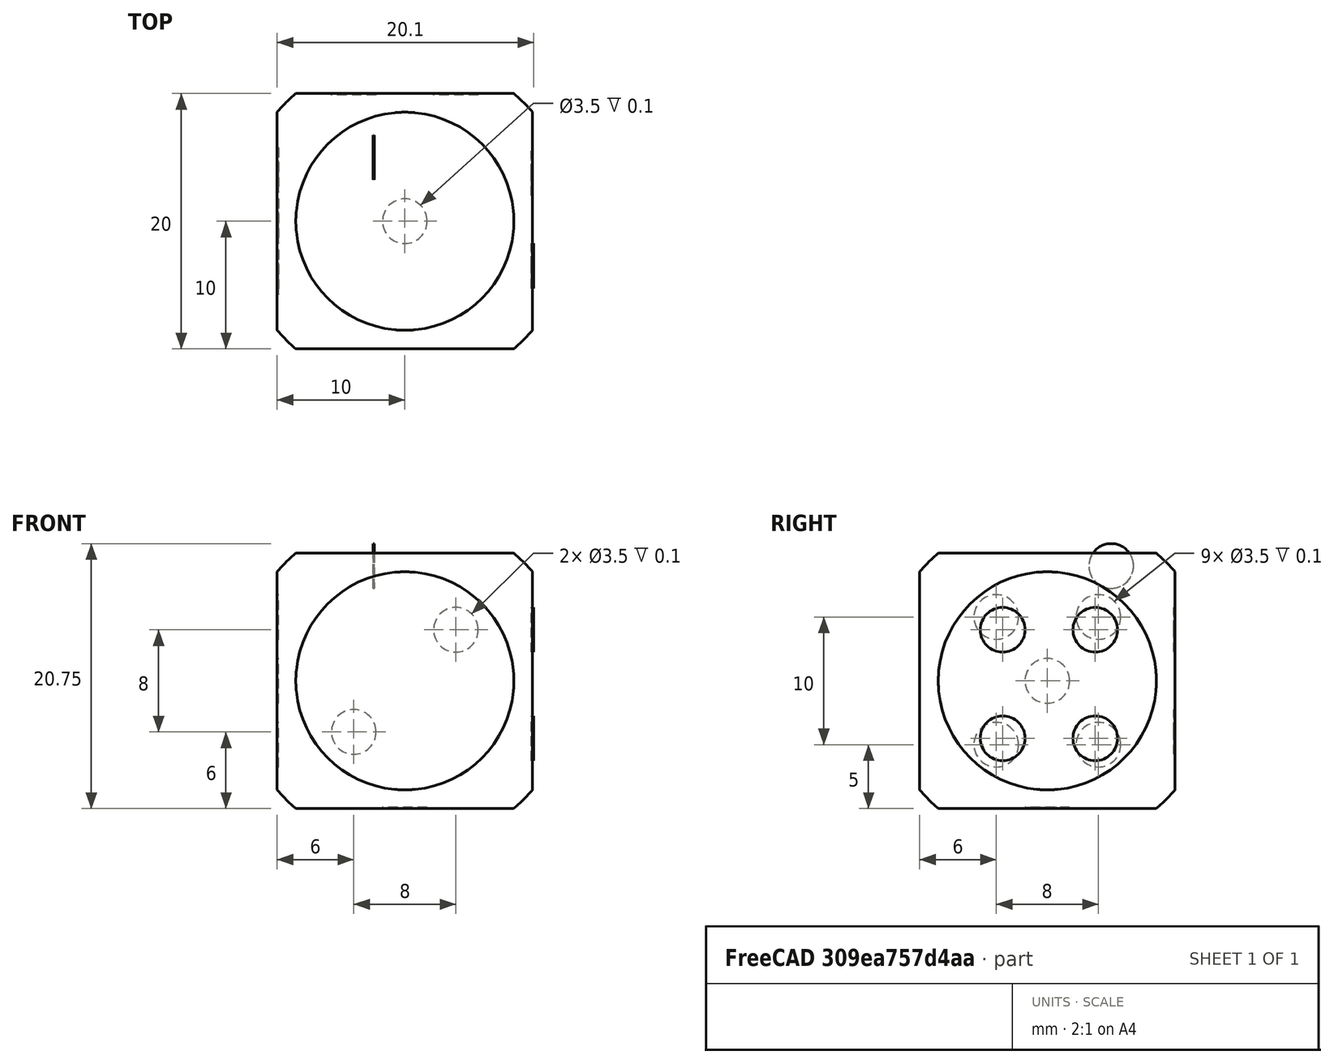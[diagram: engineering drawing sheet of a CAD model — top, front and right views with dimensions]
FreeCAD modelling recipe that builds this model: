
FCSTD DOCUMENT  (FreeCAD 0.21R33694 (Git))
Label: prodriguez_exercici2
License: All rights reserved
LicenseURL: https://en.wikipedia.org/wiki/All_rights_reserved
objects: Part::Cylinder×11, Part::Cut×10, Part::FeaturePython×4, Part::Box×1, Part::Sphere×1, Part::Fillet×1, Part::MultiCommon×1
note: 25 computed .brp shape members not serialized (recipe doc carries the construction recipe); baked Part::Feature solids carry a one-line shape summary decoded from their .brp

FEATURE [Part::Box] Box  label="Cub"
  AttacherType = Attacher::AttachEngine3D
  Height = 20
  Length = 20
  Width = 20
FEATURE [Part::Sphere] Sphere  label="Esfera"
  Angle1 = -90
  Angle2 = 90
  Angle3 = 360
  AttacherType = Attacher::AttachEngine3D
  Placement = pos=(10,10,10) rot=(0,0,1;0rad)
  Radius = 13.15
  expr: .Placement.Base.x = 10
  expr: .Placement.Base.y = 10
  expr: .Placement.Base.z = 10
FEATURE [Part::Fillet] Fillet
  Base = -> Box
  Edges = 12 edges r=1.5: [Edge1,Edge2,Edge3,Edge4,Edge5,Edge6,Edge7,Edge8,Edge9,Edge10,Edge11,Edge12]
FEATURE [Part::Cylinder] Cylinder  label="Cilindre"
  Angle = 360
  AttacherType = Attacher::AttachEngine3D
  FirstAngle = 0
  Height = 0.1
  Placement = pos=(7.5,15,19) rot=(0,1,0;1.5708rad)
  Radius = 1.75
  SecondAngle = 0
  expr: .Placement.Base.x = 7.5
  expr: .Placement.Base.y = 15
  expr: .Placement.Base.z = 19
  expr: .Placement.Rotation.Pitch = 90
  expr: .Placement.Rotation.Roll = 90
  expr: .Placement.Rotation.Yaw = 90
FEATURE [Part::FeaturePython] Array  # Draft array (typed FeaturePython)
  AlwaysSyncPlacement = false
  Angle = 360
  ArrayType = 0
  Axis = (0,0,1)
  Base = -> Cylinder
  Center = (0,0,0)
  Count = 6
  ExpandArray = false
  Fuse = false
  IntervalAxis = (0,0,0)
  IntervalX = (5.5,0,0)
  IntervalY = (0,-5,0)
  IntervalZ = (0,0,100)
  NumberCircles = 3
  NumberPolar = 5
  NumberX = 2
  NumberY = 3
  NumberZ = 1
  Placement = pos=(0,0,1) rot=(0,0,1;0rad)
  PlacementList = 6 placements: [(7.5,15,19),(7.5,10,19),(7.5,5,19),(13,15,19),(13,10,19),(13,5,19)]
  RadialDistance = 50
  ScaleList = (6) [(1,1,1),(1,1,1),(1,1,1),(1,1,1),(1,1,1),(1,1,1)]
  Symmetry = 1
  TangentialDistance = 25
  expr: .Placement.Base.x = 0
  expr: .Placement.Base.z = 1
FEATURE [Part::Cylinder] Cylinder001  label="Cilindre001"
  Angle = 360
  AttacherType = Attacher::AttachEngine3D
  FirstAngle = 0
  Height = 0.1
  Placement = pos=(20,6.5,14) rot=(0,1,0;1.5708rad)
  Radius = 1.75
  SecondAngle = 0
  expr: .Placement.Base.x = 20
  expr: .Placement.Base.y = 6.5
  expr: .Placement.Base.z = 14
  expr: .Placement.Rotation.Pitch = 90
  expr: .Placement.Rotation.Roll = 0
FEATURE [Part::MultiCommon] Common
  Shapes = -> [Sphere,Fillet]
FEATURE [Part::FeaturePython] Array001  # Draft array (typed FeaturePython)
  AlwaysSyncPlacement = false
  Angle = 360
  ArrayType = 0
  Axis = (0,0,1)
  Base = -> Cylinder001
  Center = (0,0,0)
  Count = 8
  ExpandArray = false
  Fuse = false
  IntervalAxis = (0,0,0)
  IntervalX = (0,0,0)
  IntervalY = (0,7.25,0)
  IntervalZ = (0,0,-8.5)
  NumberCircles = 3
  NumberPolar = 5
  NumberX = 2
  NumberY = 2
  NumberZ = 2
  Placement = pos=(-0.1,0,0) rot=(0,0,1;0rad)
  PlacementList = 8 placements: [(20,6.5,14),(20,6.5,5.5),(20,13.75,14),(20,13.75,5.5),(20,6.5,14),(20,6.5,5.5),(20,13.75,14),(20,13.75,5.5)]
  RadialDistance = 50
  ScaleList = (8) [(1,1,1),(1,1,1),(1,1,1),(1,1,1),(1,1,1),(1,1,1),(1,1,1),(1,1,1)]
  Symmetry = 1
  TangentialDistance = 25
  expr: .Placement.Base.x = -0.1
FEATURE [Part::Cut] Cut
  Base = -> Common
  Tool = -> Array
FEATURE [Part::Cut] Cut001
  Base = -> Cut
  Tool = -> Array001
FEATURE [Part::Cylinder] Cylinder002  label="Cilindre002"
  Angle = 360
  AttacherType = Attacher::AttachEngine3D
  FirstAngle = 0
  Height = 0.1
  Placement = pos=(10,0,10) rot=(1,0,0;1.5708rad)
  Radius = 1.75
  SecondAngle = 0
  expr: .Placement.Base.x = 10
  expr: .Placement.Base.y = 0
  expr: .Placement.Base.z = 10
  expr: .Placement.Rotation.Pitch = 0
  expr: .Placement.Rotation.Roll = 90
FEATURE [Part::Cut] Cut002
  Base = -> Cut001
  Tool = -> Cylinder002
FEATURE [Part::Cylinder] Cylinder003  label="Cilindre003"
  Angle = 360
  AttacherType = Attacher::AttachEngine3D
  FirstAngle = 0
  Height = 0.1
  Placement = pos=(6,0,6) rot=(1,0,0;1.5708rad)
  Radius = 1.75
  SecondAngle = 0
  expr: .Placement.Base.x = 6
  expr: .Placement.Base.y = 0
  expr: .Placement.Base.z = 6
  expr: .Placement.Rotation.Roll = 90
FEATURE [Part::Cut] Cut003
  Base = -> Cut002
  Tool = -> Cylinder003
FEATURE [Part::Cylinder] Cylinder004  label="Cilindre004"
  Angle = 360
  AttacherType = Attacher::AttachEngine3D
  FirstAngle = 0
  Height = 0.1
  Placement = pos=(14,0,14) rot=(1,0,0;1.5708rad)
  Radius = 1.75
  SecondAngle = 0
  expr: .Placement.Base.x = 14
  expr: .Placement.Base.z = 14
  expr: .Placement.Rotation.Roll = 90
FEATURE [Part::Cut] Cut004
  Base = -> Cut003
  Tool = -> Cylinder004
FEATURE [Part::Cylinder] Cylinder005  label="Cilindre005"
  Angle = 360
  AttacherType = Attacher::AttachEngine3D
  FirstAngle = 0
  Height = 0.1
  Placement = pos=(10,10,0) rot=(0,0,1;0rad)
  Radius = 1.75
  SecondAngle = 0
  expr: .Placement.Base.x = 10
  expr: .Placement.Base.y = 10
FEATURE [Part::Cut] Cut005
  Base = -> Cut004
  Tool = -> Cylinder005
FEATURE [Part::Cylinder] Cylinder006  label="Cilindre006"
  Angle = 360
  AttacherType = Attacher::AttachEngine3D
  FirstAngle = 0
  Height = 0.1
  Placement = pos=(6,20,6) rot=(1,0,0;1.5708rad)
  Radius = 1.75
  SecondAngle = 0
  expr: .Placement.Base.x = 6
  expr: .Placement.Base.y = 20
  expr: .Placement.Base.z = 6
  expr: .Placement.Rotation.Roll = 90
FEATURE [Part::Cylinder] Cylinder007  label="Cilindre007"
  Angle = 360
  AttacherType = Attacher::AttachEngine3D
  FirstAngle = 0
  Height = 0.1
  Placement = pos=(0,10,10) rot=(0,1,0;1.5708rad)
  Radius = 1.75
  SecondAngle = 0
  expr: .Placement.Base.x = 0
  expr: .Placement.Base.y = 10
  expr: .Placement.Base.z = 10
  expr: .Placement.Rotation.Pitch = 90
FEATURE [Part::Cylinder] Cylinder008  label="Cilindre008"
  Angle = 360
  AttacherType = Attacher::AttachEngine3D
  FirstAngle = 0
  Height = 0.1
  Placement = pos=(14,20,14) rot=(1,0,0;1.5708rad)
  Radius = 1.75
  SecondAngle = 0
  expr: .Placement.Base.x = 14
  expr: .Placement.Base.y = 20
  expr: .Placement.Base.z = 14
  expr: .Placement.Rotation.Roll = 90
FEATURE [Part::Cut] Cut006
  Base = -> Cut005
  Tool = -> Cylinder006
FEATURE [Part::Cut] Cut007
  Base = -> Cut006
  Tool = -> Cylinder008
FEATURE [Part::Cylinder] Cylinder009  label="Cilindre009"
  Angle = 360
  AttacherType = Attacher::AttachEngine3D
  FirstAngle = 0
  Height = 0.1
  Placement = pos=(0,6,15) rot=(0,1,0;1.5708rad)
  Radius = 1.75
  SecondAngle = 0
  expr: .Placement.Base.x = 0
  expr: .Placement.Base.y = 6
  expr: .Placement.Base.z = 15
  expr: .Placement.Rotation.Pitch = 90
FEATURE [Part::FeaturePython] Array002  # Draft array (typed FeaturePython)
  AlwaysSyncPlacement = false
  Angle = 360
  ArrayType = 0
  Axis = (0,0,1)
  Base = -> Cylinder009
  Center = (0,0,0)
  Count = 4
  ExpandArray = false
  Fuse = false
  IntervalAxis = (0,0,0)
  IntervalX = (5,0,0)
  IntervalY = (0,8,0)
  IntervalZ = (0,0,-10)
  NumberCircles = 3
  NumberPolar = 5
  NumberX = 1
  NumberY = 2
  NumberZ = 2
  PlacementList = 4 placements: [(0,6,15),(0,6,5),(0,14,15),(0,14,5)]
  RadialDistance = 50
  ScaleList = (4) [(1,1,1),(1,1,1),(1,1,1),(1,1,1)]
  Symmetry = 1
  TangentialDistance = 25
FEATURE [Part::Cut] Cut008
  Base = -> Cut007
  Tool = -> Cylinder007
FEATURE [Part::Cut] Cut009
  Base = -> Cut008
  Tool = -> Array002
FEATURE [Part::Cylinder] Cylinder010  label="Cilindre010"
  Angle = 360
  AttacherType = Attacher::AttachEngine3D
  FirstAngle = 0
  Height = 0.1
  Placement = pos=(20,6.5,5.5) rot=(0,1,0;1.5708rad)
  Radius = 1.75
  SecondAngle = 0
  expr: .Placement.Base.x = 20
  expr: .Placement.Base.y = 6.5
  expr: .Placement.Base.z = 5.5
  expr: .Placement.Rotation.Pitch = 90
  expr: .Placement.Rotation.Roll = 0
FEATURE [Part::FeaturePython] Array003  # Draft array (typed FeaturePython)
  AlwaysSyncPlacement = false
  Angle = 360
  ArrayType = 0
  Axis = (0,0,1)
  Base = -> Cylinder010
  Center = (0,0,0)
  Count = 1
  ExpandArray = false
  Fuse = false
  IntervalAxis = (0,0,0)
  IntervalX = (10,0,0)
  IntervalY = (10,0,20)
  IntervalZ = (0,0,10)
  NumberCircles = 3
  NumberPolar = 5
  NumberX = 0
  NumberY = 2
  NumberZ = 2
  PlacementList = 1 placements: [(20,6.5,5.5)]
  RadialDistance = 50
  ScaleList = (1) [(1,1,1)]
  Symmetry = 1
  TangentialDistance = 25
